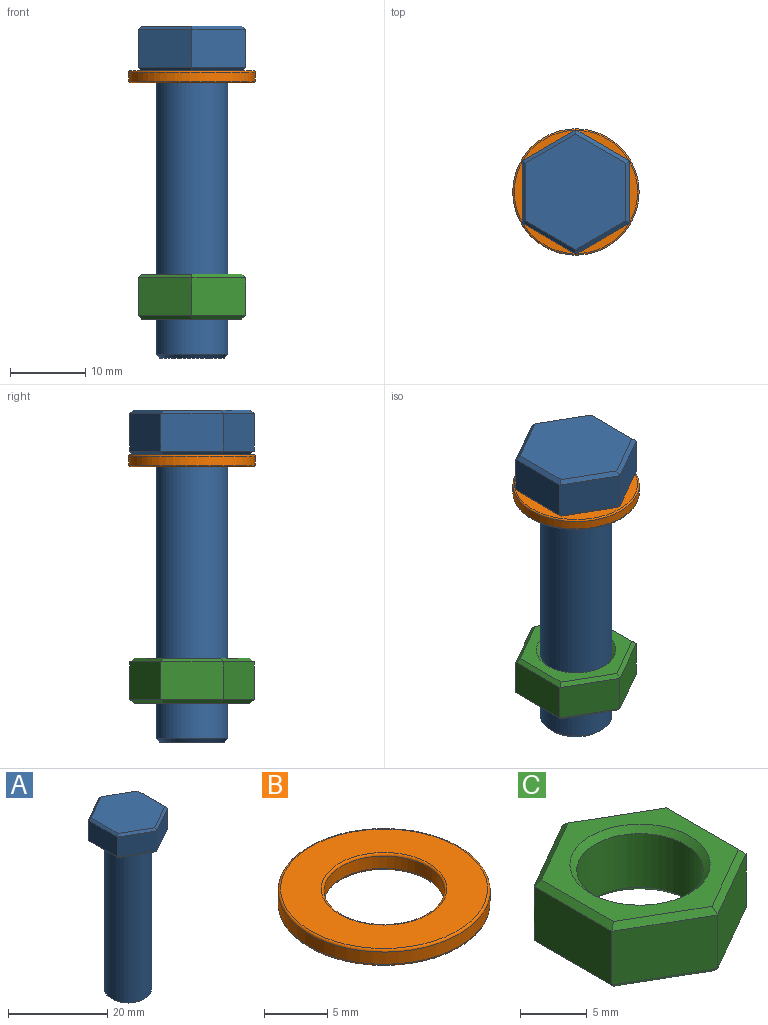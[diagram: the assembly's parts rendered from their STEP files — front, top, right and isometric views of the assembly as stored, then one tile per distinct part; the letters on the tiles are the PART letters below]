
ASSEMBLY  parts=3 mates=2
PART A: 22 faces, bbox 14.3x16.5x44.1 mm
  f0: plane 7.14x5.44mm, normal (0.5,0.87,0), area 44.6mm2, adj f1,f5,f7,f11,f15,f21
  f1: plane 7.14x4.94mm, normal (-0.5,0.87,0), area 40.7mm2, adj f0,f2,f15,f19
  f2: plane 8.25x4.94mm, normal (-1,0,0), area 40.7mm2, adj f1,f3,f14,f17
  f3: plane 7.14x4.94mm, normal (-0.5,-0.87,0), area 40.7mm2, adj f2,f4,f13,f16
  f4: plane 7.14x4.94mm, normal (0.5,-0.87,0), area 40.7mm2, adj f3,f5,f12,f18
  f5: plane 8.25x4.94mm, normal (1,0,0), area 40.7mm2, adj f0,f4,f11,f20
  f6: plane 15.32x13.27mm, normal (0,0,1), area 152.5mm2, adj f16,f17,f18,f19,f20,f21
  f7: plane 15.62x13.27mm, normal (0,0,-1), area 85mm2, adj f0,f8,f11,f12,f13,f14,f15
  f8: cylinder r=4.76mm len=37.59mm, axis (0,0,1), area 1124.9mm2, adj f7,f10
  f9: plane 8.51x8.51mm, normal (0,0,-1), area 56.9mm2, adj f10
  f10: cone r=4.76mm half-angle=45deg, axis (0,0,1), area 20.4mm2, adj f8,f9
  f11: plane 8.54x0.51mm, normal (0.71,0,-0.71), area 5.9mm2, adj f0,f5,f7,f12
  f12: plane 7.14x4.42mm, normal (0.35,-0.61,-0.71), area 5.7mm2, adj f4,f7,f11,f13
  f13: plane 7.14x4.42mm, normal (-0.35,-0.61,-0.71), area 5.7mm2, adj f3,f7,f12,f14
  f14: plane 8.25x0.51mm, normal (-0.71,0,-0.71), area 5.7mm2, adj f2,f7,f13,f15
  f15: plane 7.65x4.42mm, normal (-0.35,0.61,-0.71), area 5.9mm2, adj f0,f1,f7,f14
  f16: plane 7.14x4.42mm, normal (-0.35,-0.61,0.71), area 5.7mm2, adj f3,f6,f17,f18
  f17: plane 8.25x0.51mm, normal (-0.71,0,0.71), area 5.7mm2, adj f2,f6,f16,f19
  f18: plane 7.14x4.42mm, normal (0.35,-0.61,0.71), area 5.7mm2, adj f4,f6,f16,f20
  f19: plane 7.14x4.42mm, normal (-0.35,0.61,0.71), area 5.7mm2, adj f1,f6,f17,f21
  f20: plane 8.25x0.51mm, normal (0.71,0,0.71), area 5.7mm2, adj f5,f6,f18,f21
  f21: plane 7.14x4.42mm, normal (0.35,0.61,0.71), area 5.7mm2, adj f0,f6,f19,f20
PART B: 8 faces, bbox 18.1x18.1x1.6 mm
  f0: cylinder r=4.76mm len=9.53mm, axis (0,0,-1), area 35.3mm2, adj f4,f6
  f1: cylinder r=8.38mm len=16.76mm, axis (0,0,-1), area 62.2mm2, adj f5,f7
  f2: plane 16.36x16.36mm, normal (0,0,1), area 132.7mm2, adj f6,f7
  f3: plane 16.36x16.36mm, normal (0,0,-1), area 132.7mm2, adj f4,f5
  f4: torus R=4.97mm, axis (0,0,1), area 9.7mm2, adj f0,f3
  f5: torus R=8.18mm, axis (0,0,1), area 16.7mm2, adj f1,f3
  f6: torus R=4.97mm, axis (0,0,1), area 9.7mm2, adj f0,f2
  f7: torus R=8.18mm, axis (0,0,1), area 16.7mm2, adj f1,f2
PART C: 23 faces, bbox 14.3x16.5x6 mm
  f0: plane 7.14x4.94mm, normal (0.5,0.87,0), area 40.7mm2, adj f1,f6,f11,f19
  f1: plane 7.14x4.94mm, normal (-0.5,0.87,0), area 40.7mm2, adj f0,f2,f13,f21
  f2: plane 8.25x4.94mm, normal (-1,0,0), area 40.7mm2, adj f1,f3,f15,f22
  f3: plane 7.14x4.94mm, normal (-0.5,-0.87,0), area 40.7mm2, adj f2,f4,f16,f20
  f4: plane 7.14x4.94mm, normal (0.5,-0.87,0), area 40.7mm2, adj f3,f6,f14,f18
  f5: cylinder r=4.76mm len=9.53mm, axis (0,0,-1), area 147.7mm2, adj f9,f10
  f6: plane 8.25x4.94mm, normal (1,0,0), area 40.7mm2, adj f0,f4,f12,f17
  f7: plane 15.32x13.27mm, normal (0,0,1), area 65.3mm2, adj f10,f17,f18,f19,f20,f21,f22
  f8: plane 15.32x13.27mm, normal (0,0,-1), area 65.3mm2, adj f9,f11,f12,f13,f14,f15,f16
  f9: cone r=5.27mm half-angle=45deg, axis (0,0,-1), area 22.6mm2, adj f5,f8
  f10: cone r=4.76mm half-angle=45deg, axis (0,0,1), area 22.6mm2, adj f5,f7
  f11: plane 7.14x4.42mm, normal (0.35,0.61,-0.71), area 5.7mm2, adj f0,f8,f12,f13
  f12: plane 8.25x0.51mm, normal (0.71,0,-0.71), area 5.7mm2, adj f6,f8,f11,f14
  f13: plane 7.14x4.42mm, normal (-0.35,0.61,-0.71), area 5.7mm2, adj f1,f8,f11,f15
  f14: plane 7.14x4.42mm, normal (0.35,-0.61,-0.71), area 5.7mm2, adj f4,f8,f12,f16
  f15: plane 8.25x0.51mm, normal (-0.71,0,-0.71), area 5.7mm2, adj f2,f8,f13,f16
  f16: plane 7.14x4.42mm, normal (-0.35,-0.61,-0.71), area 5.7mm2, adj f3,f8,f14,f15
  f17: plane 8.25x0.51mm, normal (0.71,0,0.71), area 5.7mm2, adj f6,f7,f18,f19
  f18: plane 7.14x4.42mm, normal (0.35,-0.61,0.71), area 5.7mm2, adj f4,f7,f17,f20
  f19: plane 7.14x4.42mm, normal (0.35,0.61,0.71), area 5.7mm2, adj f0,f7,f17,f21
  f20: plane 7.14x4.42mm, normal (-0.35,-0.61,0.71), area 5.7mm2, adj f3,f7,f18,f22
  f21: plane 7.14x4.42mm, normal (-0.35,0.61,0.71), area 5.7mm2, adj f1,f7,f19,f22
  f22: plane 8.25x0.51mm, normal (-0.71,0,0.71), area 5.7mm2, adj f2,f7,f20,f21
PLACE A t=(31.2,-13.86,27.3)mm fixed
PLACE B t=(31.2,-13.86,25.71)mm
PLACE C t=(31.34,-14.07,-5.63)mm
MATE slider C.f5 <-> A.f8  axis (0,0,1) through (31.2,-13.86,-0.18)mm
MATE fastened B.f0 <-> A.f8  axis (0,0,1) through (31.2,-13.86,27.3)mm
